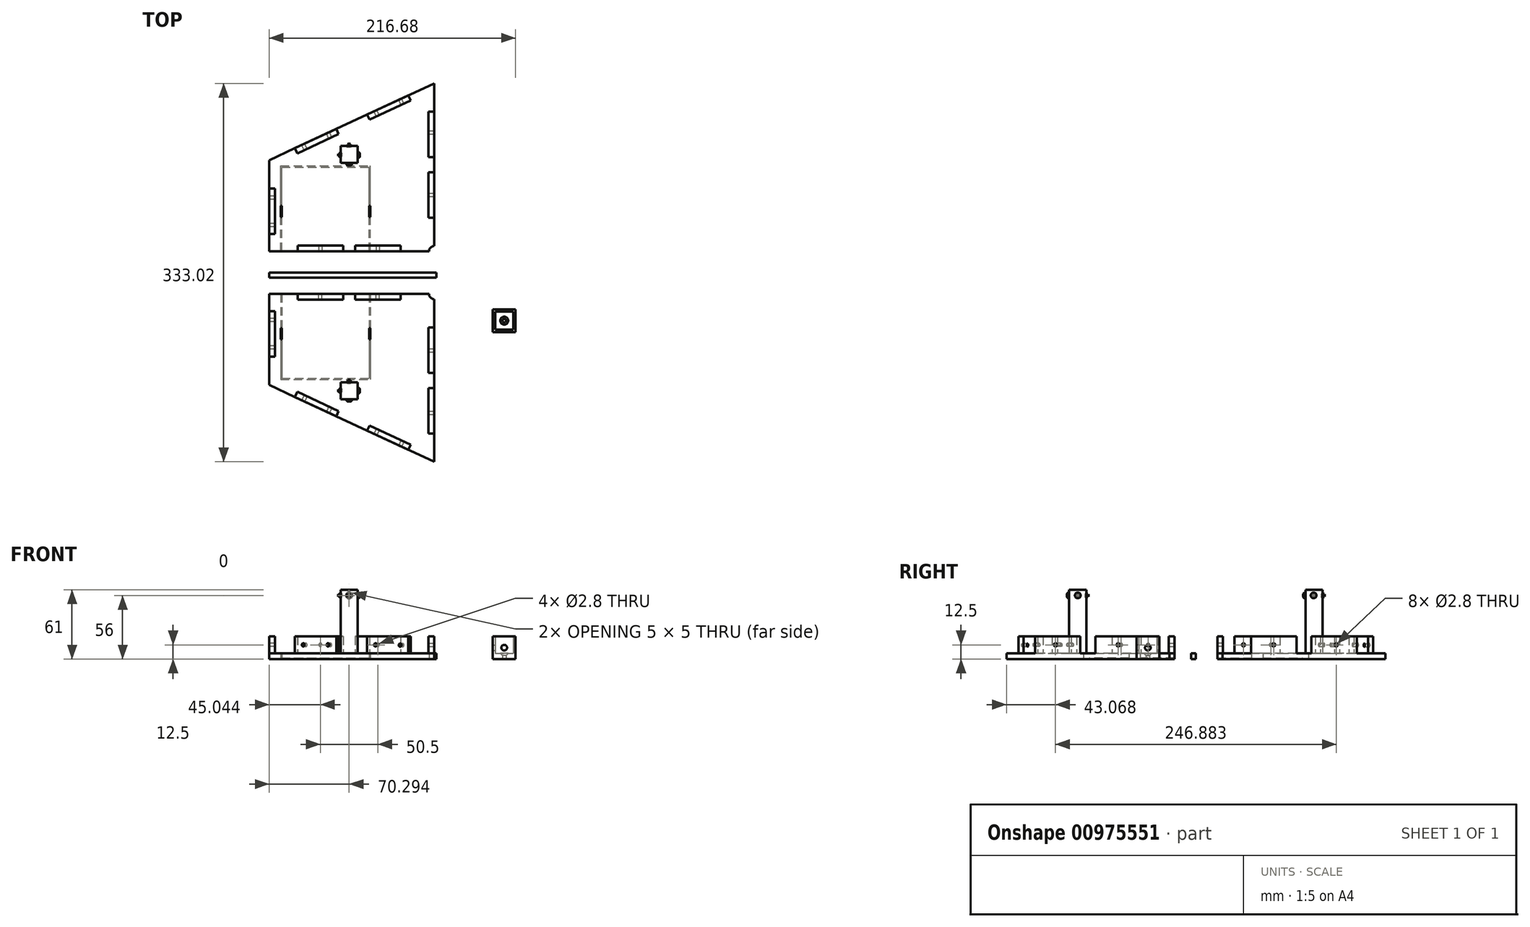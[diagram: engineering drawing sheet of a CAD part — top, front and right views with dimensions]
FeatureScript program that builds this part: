
annotation { "Feature Type Name" : "Feature", "Feature Type Description" : "" }
export const myFeature = defineFeature(function(context is Context, id is Id, definition is map)
    precondition{}
    {
        {
            var Q0;
            Q0=qCreatedBy(makeId("Top.planeOp"),FACE);
            var sketch = newSketch(context, id + "F0", { "sketchPlane" : qUnion([Q0])});
            skLineSegment(sketch, "E0", {"start": v(-54.05, 34.89) * mm, "end": v(90.95, 34.89) * mm, "construction": true});
            skLineSegment(sketch, "E1", {"start": v(90.95, 34.89) * mm, "end": v(-54.05, 34.89) * mm, "construction": true});
            skLineSegment(sketch, "E2", {"start": v(-54.05, 34.89) * mm, "end": v(-54.05, -45.11) * mm, "construction": true});
            skLineSegment(sketch, "E3", {"start": v(-54.05, -45.11) * mm, "end": v(90.95, -112.75) * mm});
            skLineSegment(sketch, "E4", {"start": v(90.95, -112.75) * mm, "end": v(90.95, 34.89) * mm, "construction": true});
            skLineSegment(sketch, "E5", {"start": v(-54.05, 34.89) * mm, "end": v(-54.05, -45.11) * mm});
            skLineSegment(sketch, "E6", {"start": v(90.95, 34.89) * mm, "end": v(90.95, -112.75) * mm});
            skLineSegment(sketch, "E7", {"start": v(-54.05, 34.89) * mm, "end": v(90.95, 34.89) * mm});
            skCircle(sketch, "E8", {"center": v(90.95, 34.89) * mm, "radius": 4.5 * mm});
            skSolve(sketch);
        }
        {
            var Q0;
            Q0=makeQuery(id+"F0.imprint","IMPRINT",FACE,{"disambiguationData":[TD([[makeQuery(id+"F0.imprint","IMPRINT",EDGE,{"derivedFrom":sQuery(id+"F0.wireOp",EDGE,"E3")}),1.0]])]});
            extrude(context, id + "F1", {"entities" : qUnion([Q0]), "depth" : 5 * mm, "offsetDistance" : 25 * mm});
        }
        {
            var Q0;
            Q0=makeQuery(id+"F1.opExtrude","CAP_FACE",FACE,{"disambiguationData":[OSD([sQuery(id+"F0.wireOp",EDGE,"E3"),sQuery(id+"F0.wireOp",EDGE,"E5"),sQuery(id+"F0.wireOp",EDGE,"E6"),sQuery(id+"F0.wireOp",EDGE,"E7")])],"isStart":false});
            var sketch = newSketch(context, id + "F2", { "sketchPlane" : qUnion([Q0])});
            skLineSegment(sketch, "E9.bottom", {"start": v(-54.05, 19.89) * mm, "end": v(-49.05, 19.89) * mm});
            skLineSegment(sketch, "E9.top", {"start": v(-54.05, -20.11) * mm, "end": v(-49.05, -20.11) * mm});
            skLineSegment(sketch, "E9.left", {"start": v(-54.05, 19.89) * mm, "end": v(-54.05, -20.11) * mm});
            skLineSegment(sketch, "E9.right", {"start": v(-49.05, 19.89) * mm, "end": v(-49.05, -20.11) * mm});
            skLineSegment(sketch, "E10.bottom", {"start": v(-31.39, -55.68) * mm, "end": v(4.86, -72.59) * mm});
            skLineSegment(sketch, "E10.top", {"start": v(-29.28, -51.15) * mm, "end": v(6.98, -68.06) * mm});
            skLineSegment(sketch, "E10.left", {"start": v(-31.39, -55.68) * mm, "end": v(-29.28, -51.15) * mm});
            skLineSegment(sketch, "E10.right", {"start": v(4.86, -72.59) * mm, "end": v(6.98, -68.06) * mm});
            skLineSegment(sketch, "E11.bottom", {"start": v(32.05, -85.28) * mm, "end": v(68.3, -102.18) * mm});
            skLineSegment(sketch, "E11.top", {"start": v(34.16, -80.74) * mm, "end": v(70.41, -97.65) * mm});
            skLineSegment(sketch, "E11.left", {"start": v(32.05, -85.28) * mm, "end": v(34.16, -80.74) * mm});
            skLineSegment(sketch, "E11.right", {"start": v(68.3, -102.18) * mm, "end": v(70.41, -97.65) * mm});
            skLineSegment(sketch, "E12.bottom", {"start": v(90.95, -87.75) * mm, "end": v(85.95, -87.75) * mm});
            skLineSegment(sketch, "E12.top", {"start": v(90.95, -47.75) * mm, "end": v(85.95, -47.75) * mm});
            skLineSegment(sketch, "E12.left", {"start": v(90.95, -87.75) * mm, "end": v(90.95, -47.75) * mm});
            skLineSegment(sketch, "E12.right", {"start": v(85.95, -87.75) * mm, "end": v(85.95, -47.75) * mm});
            skLineSegment(sketch, "E13.bottom", {"start": v(90.95, -34.61) * mm, "end": v(85.95, -34.61) * mm});
            skLineSegment(sketch, "E13.top", {"start": v(90.95, 5.39) * mm, "end": v(85.95, 5.39) * mm});
            skLineSegment(sketch, "E13.left", {"start": v(90.95, -34.61) * mm, "end": v(90.95, 5.39) * mm});
            skLineSegment(sketch, "E13.right", {"start": v(85.95, -34.61) * mm, "end": v(85.95, 5.39) * mm});
            skLineSegment(sketch, "E14.bottom", {"start": v(61.45, 34.89) * mm, "end": v(21.45, 34.89) * mm});
            skLineSegment(sketch, "E14.top", {"start": v(61.45, 29.89) * mm, "end": v(21.45, 29.89) * mm});
            skLineSegment(sketch, "E14.left", {"start": v(61.45, 34.89) * mm, "end": v(61.45, 29.89) * mm});
            skLineSegment(sketch, "E14.right", {"start": v(21.45, 34.89) * mm, "end": v(21.45, 29.89) * mm});
            skLineSegment(sketch, "E15.bottom", {"start": v(10.95, 34.89) * mm, "end": v(-29.05, 34.89) * mm});
            skLineSegment(sketch, "E15.top", {"start": v(10.95, 29.89) * mm, "end": v(-29.05, 29.89) * mm});
            skLineSegment(sketch, "E15.left", {"start": v(10.95, 34.89) * mm, "end": v(10.95, 29.89) * mm});
            skLineSegment(sketch, "E15.right", {"start": v(-29.05, 34.89) * mm, "end": v(-29.05, 29.89) * mm});
            skSolve(sketch);
        }
        {
            var Q0;
            Q0 = qSketchRegion(id + "F2", true);
            extrude(context, id + "F3", {"entities" : qUnion([Q0]), "operationType" : NewBodyOperationType.ADD, "depth" : 15 * mm, "offsetDistance" : 25 * mm});
        }
        {
            var Q0;
            Q0=makeQuery(id+"F3.boolean.opBoolean","MERGE",FACE,{"derivedFrom":[makeQuery(id+"F1.opExtrude","SWEPT_FACE",FACE,{"disambiguationData":[OSD([sQuery(id+"F0.wireOp",EDGE,"E7")])]}),makeQuery(id+"F3.opExtrude","SWEPT_FACE",FACE,{"disambiguationData":[OSD([sQuery(id+"F2.wireOp",EDGE,"E14.bottom")])]}),makeQuery(id+"F3.opExtrude","SWEPT_FACE",FACE,{"disambiguationData":[OSD([sQuery(id+"F2.wireOp",EDGE,"E15.bottom")])]})]});
            var sketch = newSketch(context, id + "F4", { "sketchPlane" : qUnion([Q0])});
            skCircle(sketch, "E16", {"center": v(-41.45, 12.5) * mm, "radius": 1.4 * mm});
            skPoint(sketch, "E16.centerSnap0", {"position": v(-41.45, 20) * mm});
            skCircle(sketch, "E17", {"center": v(9.05, 12.5) * mm, "radius": 1.4 * mm});
            skPoint(sketch, "E17.centerSnap0", {"position": v(9.05, 20) * mm});
            skSolve(sketch);
        }
        {
            var Q0;
            Q0 = qSketchRegion(id + "F4", true);
            extrude(context, id + "F5", {"entities" : qUnion([Q0]), "operationType" : NewBodyOperationType.REMOVE, "oppositeDirection" : true, "depth" : 5 * mm, "offsetDistance" : 25 * mm});
        }
        {
            var Q0;
            Q0=makeQuery(id+"F3.boolean.opBoolean","MERGE",FACE,{"derivedFrom":[makeQuery(id+"F1.opExtrude","SWEPT_FACE",FACE,{"disambiguationData":[OSD([sQuery(id+"F0.wireOp",EDGE,"E5")])]}),makeQuery(id+"F3.opExtrude","SWEPT_FACE",FACE,{"disambiguationData":[OSD([sQuery(id+"F2.wireOp",EDGE,"E9.left")])]})]});
            var sketch = newSketch(context, id + "F6", { "sketchPlane" : qUnion([Q0])});
            skCircle(sketch, "E18", {"center": v(-11.89, 12.5) * mm, "radius": 1.4 * mm});
            skCircle(sketch, "E19", {"center": v(12.11, 12.5) * mm, "radius": 1.4 * mm});
            skSolve(sketch);
        }
        {
            var Q0;
            Q0 = qSketchRegion(id + "F6", true);
            extrude(context, id + "F7", {"entities" : qUnion([Q0]), "operationType" : NewBodyOperationType.REMOVE, "oppositeDirection" : true, "depth" : 5 * mm, "offsetDistance" : 25 * mm});
        }
        {
            var Q0;
            Q0=makeQuery(id+"F3.opExtrude","SWEPT_FACE",FACE,{"disambiguationData":[OSD([sQuery(id+"F2.wireOp",EDGE,"E10.bottom")])]});
            var sketch = newSketch(context, id + "F8", { "sketchPlane" : qUnion([Q0])});
            skCircle(sketch, "E20", {"center": v(3.08, 12.5) * mm, "radius": 1.4 * mm});
            skCircle(sketch, "E21", {"center": v(27.08, 12.5) * mm, "radius": 1.4 * mm});
            skSolve(sketch);
        }
        {
            var Q0;
            Q0 = qSketchRegion(id + "F8", true);
            extrude(context, id + "F9", {"entities" : qUnion([Q0]), "operationType" : NewBodyOperationType.REMOVE, "oppositeDirection" : true, "depth" : 5 * mm, "offsetDistance" : 25 * mm});
        }
        {
            var Q0;
            Q0=makeQuery(id+"F3.opExtrude","SWEPT_FACE",FACE,{"disambiguationData":[OSD([sQuery(id+"F2.wireOp",EDGE,"E11.bottom")])]});
            var sketch = newSketch(context, id + "F10", { "sketchPlane" : qUnion([Q0])});
            skCircle(sketch, "E22", {"center": v(73.08, 12.5) * mm, "radius": 1.4 * mm});
            skCircle(sketch, "E23", {"center": v(97.08, 12.3) * mm, "radius": 1.4 * mm});
            skSolve(sketch);
        }
        {
            var Q0;
            Q0 = qSketchRegion(id + "F10", true);
            extrude(context, id + "F11", {"entities" : qUnion([Q0]), "operationType" : NewBodyOperationType.REMOVE, "oppositeDirection" : true, "depth" : 5 * mm, "offsetDistance" : 25 * mm});
        }
        {
            var Q0;
            Q0=makeQuery(id+"F3.boolean.opBoolean","MERGE",FACE,{"derivedFrom":[makeQuery(id+"F1.opExtrude","SWEPT_FACE",FACE,{"disambiguationData":[OSD([sQuery(id+"F0.wireOp",EDGE,"E6")])]}),makeQuery(id+"F3.opExtrude","SWEPT_FACE",FACE,{"disambiguationData":[OSD([sQuery(id+"F2.wireOp",EDGE,"E12.left")])]}),makeQuery(id+"F3.opExtrude","SWEPT_FACE",FACE,{"disambiguationData":[OSD([sQuery(id+"F2.wireOp",EDGE,"E13.left")])]})]});
            var sketch = newSketch(context, id + "F12", { "sketchPlane" : qUnion([Q0])});
            skCircle(sketch, "E24", {"center": v(-69.68, 12.5) * mm, "radius": 1.4 * mm});
            skCircle(sketch, "E25", {"center": v(-14.61, 12.5) * mm, "radius": 1.4 * mm});
            skPoint(sketch, "E25.centerSnap0", {"position": v(-14.61, 20) * mm});
            skSolve(sketch);
        }
        {
            var Q0;
            Q0 = qSketchRegion(id + "F12", true);
            extrude(context, id + "F13", {"entities" : qUnion([Q0]), "operationType" : NewBodyOperationType.REMOVE, "oppositeDirection" : true, "depth" : 5 * mm, "offsetDistance" : 25 * mm});
        }
        {
            var Q0;
            Q0=qCreatedBy(makeId("Top.planeOp"),FACE);
            var sketch = newSketch(context, id + "F14", { "sketchPlane" : qUnion([Q0])});
            skLineSegment(sketch, "E26.bottom", {"start": v(-54.09, 49.47) * mm, "end": v(92.87, 49.47) * mm});
            skLineSegment(sketch, "E26.top", {"start": v(-54.09, 53.76) * mm, "end": v(92.87, 53.76) * mm});
            skLineSegment(sketch, "E26.left", {"start": v(-54.09, 49.47) * mm, "end": v(-54.09, 53.76) * mm});
            skLineSegment(sketch, "E26.right", {"start": v(92.87, 49.47) * mm, "end": v(92.87, 53.76) * mm});
            skSolve(sketch);
        }
        {
            var Q0;
            Q0 = qSketchRegion(id + "F14", true);
            extrude(context, id + "F15", {"entities" : qUnion([Q0]), "depth" : 5 * mm, "offsetDistance" : 25 * mm});
        }
        {
            var Q0;
            Q0=makeQuery(id+"F1.opExtrude","SWEPT_BODY",BODY,{"disambiguationData":[OSD([sQuery(id+"F0.wireOp",EDGE,"E3"),sQuery(id+"F0.wireOp",EDGE,"E5"),sQuery(id+"F0.wireOp",EDGE,"E6"),sQuery(id+"F0.wireOp",EDGE,"E7")])]});
            var Q1;
            Q1=makeQuery(id+"F15.opExtrude","SWEPT_FACE",FACE,{"disambiguationData":[OSD([sQuery(id+"F14.wireOp",EDGE,"E26.top")])]});
            mirror(context, id + "F16", {"entities" : qUnion([Q0]), "mirrorPlane" : qUnion([Q1])});
        }
        {
            var Q0;
            Q0=makeQuery(id+"F1.opExtrude","CAP_FACE",FACE,{"disambiguationData":[OSD([sQuery(id+"F0.wireOp",EDGE,"E3"),sQuery(id+"F0.wireOp",EDGE,"E5"),sQuery(id+"F0.wireOp",EDGE,"E6"),sQuery(id+"F0.wireOp",EDGE,"E7"),sQuery(id+"F0.wireOp",EDGE,"E8")])],"isStart":true});
            var sketch = newSketch(context, id + "F17", { "sketchPlane" : qUnion([Q0])});
            skLineSegment(sketch, "E27.bottom", {"start": v(-44.05, -34.89) * mm, "end": v(34.95, -34.89) * mm});
            skLineSegment(sketch, "E27.top", {"start": v(-44.05, 40.11) * mm, "end": v(34.95, 40.11) * mm});
            skLineSegment(sketch, "E27.left", {"start": v(-44.05, -34.89) * mm, "end": v(-44.05, 40.11) * mm});
            skLineSegment(sketch, "E27.right", {"start": v(34.95, -34.89) * mm, "end": v(34.95, 40.11) * mm});
            skLineSegment(sketch, "E28.bottom", {"start": v(-43.05, -34.89) * mm, "end": v(33.95, -34.89) * mm});
            skLineSegment(sketch, "E28.top", {"start": v(-43.05, 39.11) * mm, "end": v(33.95, 39.11) * mm});
            skLineSegment(sketch, "E28.left", {"start": v(-43.05, -34.89) * mm, "end": v(-43.05, 39.11) * mm});
            skLineSegment(sketch, "E28.right", {"start": v(33.95, -34.89) * mm, "end": v(33.95, 39.11) * mm});
            skLineSegment(sketch, "E29.bottom", {"start": v(-43.05, 5.11) * mm, "end": v(-44.05, 5.11) * mm});
            skLineSegment(sketch, "E29.top", {"start": v(-43.05, -4.89) * mm, "end": v(-44.05, -4.89) * mm});
            skLineSegment(sketch, "E29.left", {"start": v(-43.05, 5.11) * mm, "end": v(-43.05, -4.89) * mm});
            skLineSegment(sketch, "E29.right", {"start": v(-44.05, 5.11) * mm, "end": v(-44.05, -4.89) * mm});
            skLineSegment(sketch, "E30.bottom", {"start": v(33.95, 5.11) * mm, "end": v(34.95, 5.11) * mm});
            skLineSegment(sketch, "E30.top", {"start": v(33.95, -4.89) * mm, "end": v(34.95, -4.89) * mm});
            skLineSegment(sketch, "E30.left", {"start": v(33.95, 5.11) * mm, "end": v(33.95, -4.89) * mm});
            skLineSegment(sketch, "E30.right", {"start": v(34.95, 5.11) * mm, "end": v(34.95, -4.89) * mm});
            skSolve(sketch);
        }
        {
            var Q0;
            Q0=makeQuery(id+"F17.imprint","IMPRINT",FACE,{"disambiguationData":[TD([[makeQuery(id+"F17.imprint","IMPRINT",EDGE,{"derivedFrom":sQuery(id+"F17.wireOp",EDGE,"E27.top")}),-1.0]])]});
            var Q1;
            {var subQ5=sQuery(id+"F17.wireOp",EDGE,"E29.top");Q1=makeQuery(id+"F17.imprint","IMPRINT",FACE,{"disambiguationData":[TD([[makeQuery(id+"F17.imprint","IMPRINT",EDGE,{"derivedFrom":subQ5}),1.0]])]});}
            var Q2;
            {var subQ5=sQuery(id+"F17.wireOp",EDGE,"E30.top");Q2=makeQuery(id+"F17.imprint","IMPRINT",FACE,{"disambiguationData":[TD([[makeQuery(id+"F17.imprint","IMPRINT",EDGE,{"derivedFrom":subQ5}),-1.0]])]});}
            extrude(context, id + "F18", {"entities" : qUnion([Q0, Q1, Q2]), "operationType" : NewBodyOperationType.REMOVE, "oppositeDirection" : true, "depth" : 1 * mm, "offsetDistance" : 25 * mm});
        }
        {
            var Q0;
            Q0=makeQuery(id+"F16.opPattern","COPY",FACE,{"derivedFrom":makeQuery(id+"F1.opExtrude","CAP_FACE",FACE,{"disambiguationData":[OSD([sQuery(id+"F0.wireOp",EDGE,"E3"),sQuery(id+"F0.wireOp",EDGE,"E5"),sQuery(id+"F0.wireOp",EDGE,"E6"),sQuery(id+"F0.wireOp",EDGE,"E7"),sQuery(id+"F0.wireOp",EDGE,"E8")])],"isStart":true}),"instanceName":"1"});
            var sketch = newSketch(context, id + "F19", { "sketchPlane" : qUnion([Q0])});
            skLineSegment(sketch, "E31.bottom", {"start": v(-44.05, -72.63) * mm, "end": v(34.95, -72.63) * mm});
            skLineSegment(sketch, "E31.top", {"start": v(-44.05, -147.63) * mm, "end": v(34.95, -147.63) * mm});
            skLineSegment(sketch, "E31.left", {"start": v(-44.05, -72.63) * mm, "end": v(-44.05, -147.63) * mm});
            skLineSegment(sketch, "E31.right", {"start": v(34.95, -72.63) * mm, "end": v(34.95, -147.63) * mm});
            skLineSegment(sketch, "E32.bottom", {"start": v(-43.05, -72.63) * mm, "end": v(33.95, -72.63) * mm});
            skLineSegment(sketch, "E32.top", {"start": v(-43.05, -146.63) * mm, "end": v(33.95, -146.63) * mm});
            skLineSegment(sketch, "E32.left", {"start": v(-43.05, -72.63) * mm, "end": v(-43.05, -146.63) * mm});
            skLineSegment(sketch, "E32.right", {"start": v(33.95, -72.63) * mm, "end": v(33.95, -146.63) * mm});
            skLineSegment(sketch, "E33.bottom", {"start": v(-43.05, -112.63) * mm, "end": v(-44.05, -112.63) * mm});
            skLineSegment(sketch, "E33.top", {"start": v(-43.05, -102.63) * mm, "end": v(-44.05, -102.63) * mm});
            skLineSegment(sketch, "E33.left", {"start": v(-43.05, -112.63) * mm, "end": v(-43.05, -102.63) * mm});
            skLineSegment(sketch, "E33.right", {"start": v(-44.05, -112.63) * mm, "end": v(-44.05, -102.63) * mm});
            skLineSegment(sketch, "E34.bottom", {"start": v(34.95, -112.63) * mm, "end": v(33.95, -112.63) * mm});
            skLineSegment(sketch, "E34.top", {"start": v(34.95, -102.63) * mm, "end": v(33.95, -102.63) * mm});
            skLineSegment(sketch, "E34.left", {"start": v(34.95, -112.63) * mm, "end": v(34.95, -102.63) * mm});
            skLineSegment(sketch, "E34.right", {"start": v(33.95, -112.63) * mm, "end": v(33.95, -102.63) * mm});
            skSolve(sketch);
        }
        {
            var Q0;
            Q0=makeQuery(id+"F19.imprint","IMPRINT",FACE,{"disambiguationData":[TD([[makeQuery(id+"F19.imprint","IMPRINT",EDGE,{"derivedFrom":sQuery(id+"F19.wireOp",EDGE,"E31.top")}),1.0]])]});
            var Q1;
            {var subQ5=sQuery(id+"F19.wireOp",EDGE,"E33.top");Q1=makeQuery(id+"F19.imprint","IMPRINT",FACE,{"disambiguationData":[TD([[makeQuery(id+"F19.imprint","IMPRINT",EDGE,{"derivedFrom":subQ5}),-1.0]])]});}
            var Q2;
            {var subQ5=sQuery(id+"F19.wireOp",EDGE,"E34.top");Q2=makeQuery(id+"F19.imprint","IMPRINT",FACE,{"disambiguationData":[TD([[makeQuery(id+"F19.imprint","IMPRINT",EDGE,{"derivedFrom":subQ5}),-1.0]])]});}
            extrude(context, id + "F20", {"entities" : qUnion([Q0, Q1, Q2]), "operationType" : NewBodyOperationType.REMOVE, "oppositeDirection" : true, "depth" : 1 * mm, "offsetDistance" : 25 * mm});
        }
        {
            var Q0;
            Q0=makeQuery(id+"F19.imprint","IMPRINT",FACE,{"disambiguationData":[TD([[makeQuery(id+"F19.imprint","IMPRINT",EDGE,{"derivedFrom":sQuery(id+"F19.wireOp",EDGE,"E33.bottom")}),-1.0]])]});
            var Q1;
            Q1=makeQuery(id+"F19.imprint","IMPRINT",FACE,{"disambiguationData":[TD([[makeQuery(id+"F19.imprint","IMPRINT",EDGE,{"derivedFrom":sQuery(id+"F19.wireOp",EDGE,"E34.bottom")}),-1.0]])]});
            extrude(context, id + "F21", {"entities" : qUnion([Q0, Q1]), "operationType" : NewBodyOperationType.REMOVE, "oppositeDirection" : true, "depth" : 6 * mm, "offsetDistance" : 25 * mm});
        }
        {
            var Q0;
            Q0=makeQuery(id+"F17.imprint","IMPRINT",FACE,{"disambiguationData":[TD([[makeQuery(id+"F17.imprint","IMPRINT",EDGE,{"derivedFrom":sQuery(id+"F17.wireOp",EDGE,"E30.bottom")}),-1.0]])]});
            var Q1;
            Q1=makeQuery(id+"F17.imprint","IMPRINT",FACE,{"disambiguationData":[TD([[makeQuery(id+"F17.imprint","IMPRINT",EDGE,{"derivedFrom":sQuery(id+"F17.wireOp",EDGE,"E29.bottom")}),1.0]])]});
            extrude(context, id + "F22", {"entities" : qUnion([Q0, Q1]), "operationType" : NewBodyOperationType.REMOVE, "oppositeDirection" : true, "depth" : 6 * mm, "offsetDistance" : 25 * mm});
        }
        {
            var Q0;
            Q0=makeQuery(id+"F1.opExtrude","CAP_FACE",FACE,{"disambiguationData":[OSD([sQuery(id+"F0.wireOp",EDGE,"E3"),sQuery(id+"F0.wireOp",EDGE,"E5"),sQuery(id+"F0.wireOp",EDGE,"E6"),sQuery(id+"F0.wireOp",EDGE,"E7"),sQuery(id+"F0.wireOp",EDGE,"E8")])],"isStart":false});
            var sketch = newSketch(context, id + "F23", { "sketchPlane" : qUnion([Q0])});
            skLineSegment(sketch, "E35.bottom", {"start": v(8.7, -57.61) * mm, "end": v(23.7, -57.61) * mm});
            skLineSegment(sketch, "E35.top", {"start": v(8.7, -42.61) * mm, "end": v(23.7, -42.61) * mm});
            skLineSegment(sketch, "E35.left", {"start": v(8.7, -57.61) * mm, "end": v(8.7, -42.61) * mm});
            skLineSegment(sketch, "E35.right", {"start": v(23.7, -57.61) * mm, "end": v(23.7, -42.61) * mm});
            skPoint(sketch, "E35.middle", {"position": v(16.2, -50.11) * mm});
            skPoint(sketch, "E35.middle.positionSnap0", {"position": v(16.2, 34.89) * mm});
            skPoint(sketch, "E35.centerSnap0", {"position": v(16.2, 34.89) * mm});
            skSolve(sketch);
        }
        {
            var Q0;
            Q0 = qSketchRegion(id + "F23", true);
            extrude(context, id + "F24", {"entities" : qUnion([Q0]), "operationType" : NewBodyOperationType.ADD, "depth" : 56 * mm, "offsetDistance" : 25 * mm});
        }
        {
            var Q0;
            Q0=makeQuery(id+"F16.opPattern","COPY",FACE,{"derivedFrom":makeQuery(id+"F1.opExtrude","CAP_FACE",FACE,{"disambiguationData":[OSD([sQuery(id+"F0.wireOp",EDGE,"E3"),sQuery(id+"F0.wireOp",EDGE,"E5"),sQuery(id+"F0.wireOp",EDGE,"E6"),sQuery(id+"F0.wireOp",EDGE,"E7"),sQuery(id+"F0.wireOp",EDGE,"E8")])],"isStart":false}),"instanceName":"1"});
            var sketch = newSketch(context, id + "F25", { "sketchPlane" : qUnion([Q0])});
            skLineSegment(sketch, "E36.bottom", {"start": v(8.7, 150.13) * mm, "end": v(23.7, 150.13) * mm});
            skLineSegment(sketch, "E36.top", {"start": v(8.7, 165.13) * mm, "end": v(23.7, 165.13) * mm});
            skLineSegment(sketch, "E36.left", {"start": v(8.7, 150.13) * mm, "end": v(8.7, 165.13) * mm});
            skLineSegment(sketch, "E36.right", {"start": v(23.7, 150.13) * mm, "end": v(23.7, 165.13) * mm});
            skPoint(sketch, "E36.middle", {"position": v(16.2, 157.63) * mm});
            skPoint(sketch, "E36.middle.positionSnap0", {"position": v(16.2, 72.63) * mm});
            skPoint(sketch, "E36.centerSnap0", {"position": v(16.2, 72.63) * mm});
            skSolve(sketch);
        }
        {
            var Q0;
            Q0 = qSketchRegion(id + "F25", true);
            extrude(context, id + "F26", {"entities" : qUnion([Q0]), "operationType" : NewBodyOperationType.ADD, "depth" : 56 * mm, "offsetDistance" : 25 * mm});
        }
        {
            var Q0;
            Q0=qCreatedBy(makeId("Top.planeOp"),FACE);
            var sketch = newSketch(context, id + "F27", { "sketchPlane" : qUnion([Q0])});
            skLineSegment(sketch, "E37.bottom", {"start": v(142.59, 1.48) * mm, "end": v(162.59, 1.48) * mm});
            skLineSegment(sketch, "E37.top", {"start": v(142.59, 21.48) * mm, "end": v(162.59, 21.48) * mm});
            skLineSegment(sketch, "E37.left", {"start": v(142.59, 1.48) * mm, "end": v(142.59, 21.48) * mm});
            skLineSegment(sketch, "E37.right", {"start": v(162.59, 1.48) * mm, "end": v(162.59, 21.48) * mm});
            skPoint(sketch, "E37.middle", {"position": v(152.59, 11.48) * mm});
            skLineSegment(sketch, "E38.bottom", {"start": v(144.59, 3.48) * mm, "end": v(160.59, 3.48) * mm});
            skLineSegment(sketch, "E38.top", {"start": v(144.59, 19.48) * mm, "end": v(160.59, 19.48) * mm});
            skLineSegment(sketch, "E38.left", {"start": v(144.59, 3.48) * mm, "end": v(144.59, 19.48) * mm});
            skLineSegment(sketch, "E38.right", {"start": v(160.59, 3.48) * mm, "end": v(160.59, 19.48) * mm});
            skCircle(sketch, "E39", {"center": v(152.59, 11.48) * mm, "radius": 1.5 * mm});
            skSolve(sketch);
        }
        {
            var Q0;
            Q0=makeQuery(id+"F27.imprint","IMPRINT",FACE,{"disambiguationData":[TD([[makeQuery(id+"F27.imprint","IMPRINT",EDGE,{"derivedFrom":sQuery(id+"F27.wireOp",EDGE,"E37.bottom")}),1.0]])]});
            extrude(context, id + "F28", {"entities" : qUnion([Q0]), "depth" : 20 * mm, "offsetDistance" : 25 * mm});
        }
        {
            var Q0;
            Q0=makeQuery(id+"F27.imprint","IMPRINT",FACE,{"disambiguationData":[TD([[makeQuery(id+"F27.imprint","IMPRINT",EDGE,{"derivedFrom":sQuery(id+"F27.wireOp",EDGE,"E38.bottom")}),1.0]])]});
            extrude(context, id + "F29", {"entities" : qUnion([Q0]), "operationType" : NewBodyOperationType.ADD, "depth" : 5 * mm, "offsetDistance" : 25 * mm});
        }
        {
            var Q0;
            Q0=makeQuery(id+"F27.imprint","IMPRINT",FACE,{"disambiguationData":[TD([[makeQuery(id+"F27.imprint","IMPRINT",EDGE,{"derivedFrom":sQuery(id+"F27.wireOp",EDGE,"E39")}),1.0]])]});
            extrude(context, id + "F30", {"entities" : qUnion([Q0]), "operationType" : NewBodyOperationType.REMOVE, "oppositeDirection" : true, "depth" : 3 * mm, "offsetDistance" : 25 * mm});
        }
        {
            var Q0;
            Q0=makeQuery(id+"F28.opExtrude","SWEPT_FACE",FACE,{"disambiguationData":[OSD([sQuery(id+"F27.wireOp",EDGE,"E37.bottom")])]});
            var sketch = newSketch(context, id + "F31", { "sketchPlane" : qUnion([Q0])});
            skCircle(sketch, "E40", {"center": v(152.59, 10) * mm, "radius": 2.5 * mm});
            skPoint(sketch, "E40.centerSnap0", {"position": v(152.59, 20) * mm});
            skSolve(sketch);
        }
        {
            var Q0;
            Q0 = qSketchRegion(id + "F31", true);
            extrude(context, id + "F32", {"entities" : qUnion([Q0]), "operationType" : NewBodyOperationType.REMOVE, "oppositeDirection" : true, "depth" : 25 * mm, "offsetDistance" : 25 * mm});
        }
        {
            var Q0;
            Q0=makeQuery(id+"F28.opExtrude","SWEPT_FACE",FACE,{"disambiguationData":[OSD([sQuery(id+"F27.wireOp",EDGE,"E37.right")])]});
            var sketch = newSketch(context, id + "F33", { "sketchPlane" : qUnion([Q0])});
            skCircle(sketch, "E41", {"center": v(11.48, 10) * mm, "radius": 2.5 * mm});
            skPoint(sketch, "E41.centerSnap0", {"position": v(11.48, 20) * mm});
            skSolve(sketch);
        }
        {
            var Q0;
            Q0 = qSketchRegion(id + "F33", true);
            extrude(context, id + "F34", {"entities" : qUnion([Q0]), "operationType" : NewBodyOperationType.REMOVE, "oppositeDirection" : true, "depth" : 25 * mm, "offsetDistance" : 25 * mm});
        }
        {
            var Q0;
            Q0=makeQuery(id+"F29.opExtrude","CAP_EDGE",EDGE,{"disambiguationData":[OSD([sQuery(id+"F27.wireOp",EDGE,"E39")])],"isStart":false});
            chamfer(context, id + "F35", {"entities" : qUnion([Q0]), "width" : 2 * mm, "tangentPropagation" : true});
        }
        {
            var Q0;
            Q0=makeQuery(id+"F24.opExtrude","SWEPT_FACE",FACE,{"disambiguationData":[OSD([sQuery(id+"F23.wireOp",EDGE,"E35.right")])]});
            var sketch = newSketch(context, id + "F36", { "sketchPlane" : qUnion([Q0])});
            skCircle(sketch, "E42", {"center": v(-50.11, 56) * mm, "radius": 2.5 * mm});
            skPoint(sketch, "E42.centerSnap0", {"position": v(-50.11, 61) * mm});
            skSolve(sketch);
        }
        {
            var Q0;
            Q0 = qSketchRegion(id + "F36", true);
            extrude(context, id + "F37", {"entities" : qUnion([Q0]), "operationType" : NewBodyOperationType.ADD, "oppositeDirection" : true, "depth" : 17 * mm, "offsetDistance" : 25 * mm, "hasSecondDirection" : true, "secondDirectionOppositeDirection" : false, "secondDirectionDepth" : 2 * mm});
        }
        {
            var Q0;
            Q0=makeQuery(id+"F37.opExtrude","CAP_EDGE",EDGE,{"disambiguationData":[OSD([sQuery(id+"F36.wireOp",EDGE,"E42")])],"isStart":false});
            var Q1;
            Q1=makeQuery(id+"F37.opExtrude","CAP_EDGE",EDGE,{"disambiguationData":[OSD([sQuery(id+"F36.wireOp",EDGE,"E42")])],"isStart":true});
            fillet(context, id + "F38", {"entities" : qUnion([Q0, Q1]), "radius" : 1.5 * mm, "tangentPropagation" : true, "allowEdgeOverflow" : false});
        }
        {
            var Q0;
            Q0=makeQuery(id+"F24.opExtrude","SWEPT_FACE",FACE,{"disambiguationData":[OSD([sQuery(id+"F23.wireOp",EDGE,"E35.bottom")])]});
            var sketch = newSketch(context, id + "F39", { "sketchPlane" : qUnion([Q0])});
            skCircle(sketch, "E43", {"center": v(16.2, 56) * mm, "radius": 2.5 * mm});
            skPoint(sketch, "E43.centerSnap0", {"position": v(16.2, 61) * mm});
            skSolve(sketch);
        }
        {
            var Q0;
            Q0 = qSketchRegion(id + "F39", true);
            extrude(context, id + "F40", {"entities" : qUnion([Q0]), "operationType" : NewBodyOperationType.ADD, "oppositeDirection" : true, "depth" : 17 * mm, "offsetDistance" : 25 * mm, "hasSecondDirection" : true, "secondDirectionOppositeDirection" : false, "secondDirectionDepth" : 2 * mm});
        }
        {
            var Q0;
            Q0=makeQuery(id+"F40.opExtrude","CAP_EDGE",EDGE,{"disambiguationData":[OSD([sQuery(id+"F39.wireOp",EDGE,"E43")])],"isStart":true});
            var Q1;
            Q1=makeQuery(id+"F40.opExtrude","CAP_EDGE",EDGE,{"disambiguationData":[OSD([sQuery(id+"F39.wireOp",EDGE,"E43")])],"isStart":false});
            fillet(context, id + "F41", {"entities" : qUnion([Q0, Q1]), "radius" : 1.5 * mm, "tangentPropagation" : true, "allowEdgeOverflow" : false});
        }
        {
            var Q0;
            Q0=makeQuery(id+"F26.opExtrude","SWEPT_FACE",FACE,{"disambiguationData":[OSD([sQuery(id+"F25.wireOp",EDGE,"E36.right")])]});
            var sketch = newSketch(context, id + "F42", { "sketchPlane" : qUnion([Q0])});
            skCircle(sketch, "E44", {"center": v(157.22, 56) * mm, "radius": 2.5 * mm});
            skSolve(sketch);
        }
        {
            var Q0;
            Q0 = qSketchRegion(id + "F42", true);
            extrude(context, id + "F43", {"entities" : qUnion([Q0]), "operationType" : NewBodyOperationType.ADD, "oppositeDirection" : true, "depth" : 17 * mm, "offsetDistance" : 25 * mm, "hasSecondDirection" : true, "secondDirectionOppositeDirection" : false, "secondDirectionDepth" : 2 * mm});
        }
        {
            var Q0;
            Q0=makeQuery(id+"F43.opExtrude","CAP_EDGE",EDGE,{"disambiguationData":[OSD([sQuery(id+"F42.wireOp",EDGE,"E44")])],"isStart":true});
            var Q1;
            Q1=makeQuery(id+"F43.opExtrude","CAP_EDGE",EDGE,{"disambiguationData":[OSD([sQuery(id+"F42.wireOp",EDGE,"E44")])],"isStart":false});
            fillet(context, id + "F44", {"entities" : qUnion([Q0, Q1]), "radius" : 1.5 * mm, "tangentPropagation" : true, "allowEdgeOverflow" : false});
        }
        {
            var Q0;
            Q0=makeQuery(id+"F26.opExtrude","SWEPT_FACE",FACE,{"disambiguationData":[OSD([sQuery(id+"F25.wireOp",EDGE,"E36.bottom")])]});
            var sketch = newSketch(context, id + "F45", { "sketchPlane" : qUnion([Q0])});
            skCircle(sketch, "E45", {"center": v(16.2, 56) * mm, "radius": 2.5 * mm});
            skPoint(sketch, "E45.centerSnap0", {"position": v(16.2, 61) * mm});
            skSolve(sketch);
        }
        {
            var Q0;
            Q0 = qSketchRegion(id + "F45", true);
            extrude(context, id + "F46", {"entities" : qUnion([Q0]), "operationType" : NewBodyOperationType.ADD, "oppositeDirection" : true, "depth" : 17 * mm, "offsetDistance" : 25 * mm, "hasSecondDirection" : true, "secondDirectionOppositeDirection" : false, "secondDirectionDepth" : 2 * mm});
        }
        {
            var Q0;
            Q0=makeQuery(id+"F46.opExtrude","CAP_EDGE",EDGE,{"disambiguationData":[OSD([sQuery(id+"F45.wireOp",EDGE,"E45")])],"isStart":true});
            var Q1;
            Q1=makeQuery(id+"F46.opExtrude","CAP_EDGE",EDGE,{"disambiguationData":[OSD([sQuery(id+"F45.wireOp",EDGE,"E45")])],"isStart":false});
            fillet(context, id + "F47", {"entities" : qUnion([Q0, Q1]), "radius" : 1.5 * mm, "tangentPropagation" : true, "allowEdgeOverflow" : false});
        }
    });
